# Revit family: irnes F100
name_source: partatom
category: Windows
revit_build: Autodesk Revit 2014 (Build: 20130308_1515(x64)
units: mm (PartAtom-declared; Revit-internal decimal feet)

## types (1)
- 1000X1000X300
    AW-Wert = 0.75m²
    Analytic Construction = <None>
    BIMobject category = Roof Window
    CatValue_Height = 1000 mm  [stored 3.28084 ft]
    CatValue_Kerb Height = 300 mm
    CatValue_Width = 1000 mm  [stored 3.28084 ft]
    Depth = 0.00
    Design country = Germany
    Edition number = 1
    IFC Classification = Window
    Manufacturer = Lamilux
    Manufacturer country = Germany
    Manufacturer name = LAMILUX
    Material main = Lamilux-White
    Material secondary = Lamilux- Plastic
    NBS Reference Code = 20-30-72
    NBS Reference Description = Roof Light And Smoke Ventilator Systems
    Nominal height = 0.00
    Nominal width = 0.00
    Product SKU = Lamilux_F100_rooflight_dome
    Product family = Daylight element, SHEV
    Product group = Rooflight dome
    QR code = http://lamilux.bimobject.com
    UNSPSC Code = 301516
    URL = http://lamilux.bimobject.com
    Uniclass 1.4 Code = JL11
    Uniclass 1.4 Description = Rooflights/Roof windows
    Uniclass 2.0 Code = SS-65-10-80-80
    Uniclass 2.0 Description = Smoke And Heat Exhaust Ventilation Systems
    Weight Net (Kg) = 0

note: [stored X ft] marks values corroborated as IEEE doubles in the binary element streams (Revit-internal decimal feet)

## geometry (parser evidence)
native form markers: Sweep x2
no freeform markers — native parametric forms only
